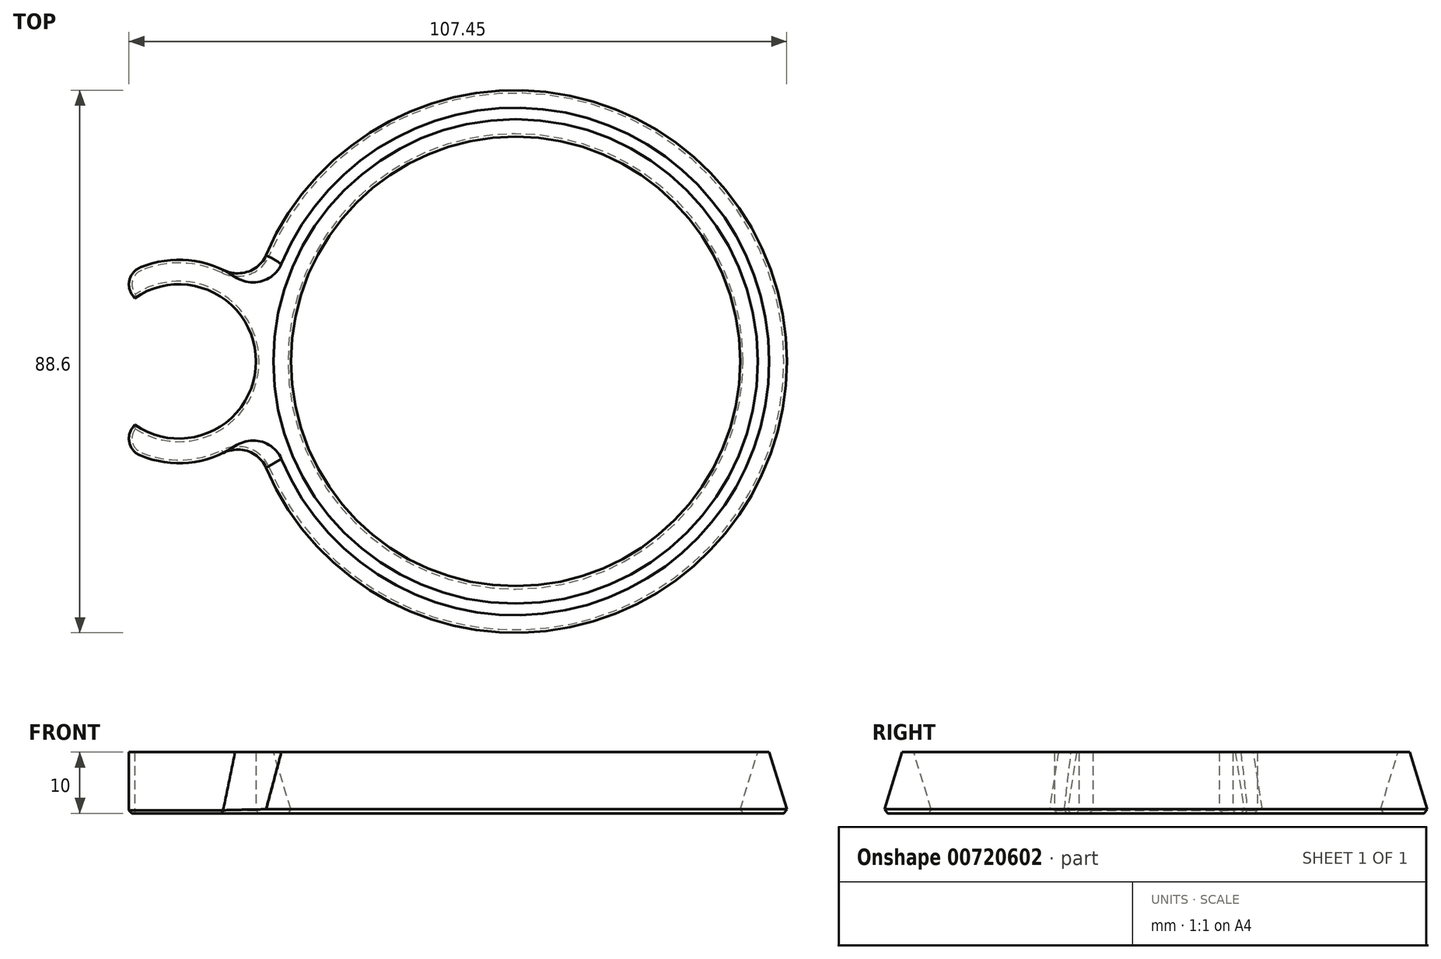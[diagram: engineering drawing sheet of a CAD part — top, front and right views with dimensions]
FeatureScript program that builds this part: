
annotation { "Feature Type Name" : "Feature", "Feature Type Description" : "" }
export const myFeature = defineFeature(function(context is Context, id is Id, definition is map)
    precondition{}
    {
        {
            var Q0;
            Q0=qCreatedBy(makeId("Top.planeOp"),FACE);
            var sketch = newSketch(context, id + "F0", { "sketchPlane" : qUnion([Q0])});
            skCircle(sketch, "E0", {"center": v(0, 0) * mm, "radius": 36.5 * mm});
            skCircle(sketch, "E1", {"center": v(0, 0) * mm, "radius": 44.5 * mm});
            skSolve(sketch);
        }
        {
            var Q0;
            Q0 = qSketchRegion(id + "F0", true);
            extrude(context, id + "F1", {"entities" : qUnion([Q0]), "depth" : 10 * mm, "offsetDistance" : 25 * mm, "hasDraft" : true, "draftAngle" : 17 * degree, "draftPullDirection" : true});
        }
        {
            var Q0;
            Q0=qCreatedBy(makeId("Top.planeOp"),FACE);
            var sketch = newSketch(context, id + "F2", { "sketchPlane" : qUnion([Q0])});
            skArc(sketch, "E2", {"start": v(-62.23, -10.32) * mm, "mid": v(-42.4, 0) * mm, "end": v(-62.23, 10.32) * mm});
            skArc(sketch, "E3", {"start": v(-39.22, 5.15) * mm, "mid": v(-49.74, 15.75) * mm, "end": v(-64.52, 13.6) * mm});
            skLineSegment(sketch, "E4", {"start": v(-62.23, 10.32) * mm, "end": v(-64.52, 13.6) * mm});
            skLineSegment(sketch, "E5", {"start": v(-64.52, 13.6) * mm, "end": v(-64.52, -13.6) * mm, "construction": true});
            skLineSegment(sketch, "E6", {"start": v(-64.52, -13.6) * mm, "end": v(-62.23, -10.32) * mm});
            skArc(sketch, "E7.0", {"start": v(-39.22, 5.15) * mm, "mid": v(-39.56, 0) * mm, "end": v(-39.22, -5.15) * mm});
            skArc(sketch, "E8.trimOffspring", {"start": v(-64.52, -13.6) * mm, "mid": v(-49.74, -15.75) * mm, "end": v(-39.22, -5.15) * mm});
            skSolve(sketch);
        }
        {
            var Q0;
            Q0=makeQuery(id+"F2.imprint","IMPRINT",FACE,{"disambiguationData":[TD([[makeQuery(id+"F2.imprint","IMPRINT",EDGE,{"derivedFrom":sQuery(id+"F2.wireOp",EDGE,"E2")}),-1.0]])]});
            var Q1;
            Q1=sQuery(id+"F2.wireOp",EDGE,"E5");
            extrude(context, id + "F3", {"entities" : qUnion([Q0]), "operationType" : NewBodyOperationType.ADD, "surfaceOperationType" : NewSurfaceOperationType.ADD, "surfaceEntities" : qUnion([Q1]), "depth" : 10 * mm, "offsetDistance" : 25 * mm});
        }
        {
            var Q0;
            Q0=qCreatedBy(makeId("Top.planeOp"),FACE);
            var sketch = newSketch(context, id + "F4", { "sketchPlane" : qUnion([Q0])});
            skArc(sketch, "E9.0", {"start": v(-62.23, -10.32) * mm, "mid": v(-42.4, 0) * mm, "end": v(-62.23, 10.32) * mm});
            skLineSegment(sketch, "E10", {"start": v(-62.23, 10.32) * mm, "end": v(-62.23, -10.32) * mm});
            skSolve(sketch);
        }
        {
            var Q0;
            Q0 = qSketchRegion(id + "F4", true);
            extrude(context, id + "F5", {"entities" : qUnion([Q0]), "operationType" : NewBodyOperationType.REMOVE, "depth" : 25 * mm, "offsetDistance" : 25 * mm});
        }
        {
            var Q0;
            Q0=makeQuery(id+"F3.boolean.opBoolean","INTERSECT",EDGE,{"derivedFrom":[makeQuery(id+"F1.opExtrude","SWEPT_FACE",FACE,{"disambiguationData":[OSD([sQuery(id+"F0.wireOp",EDGE,"E1")])]}),makeQuery(id+"F3.opExtrude","SWEPT_FACE",FACE,{"disambiguationData":[OSD([sQuery(id+"F2.wireOp",EDGE,"E8.trimOffspring")])]})]});
            var Q1;
            Q1=makeQuery(id+"F3.boolean.opBoolean","INTERSECT",EDGE,{"derivedFrom":[makeQuery(id+"F1.opExtrude","SWEPT_FACE",FACE,{"disambiguationData":[OSD([sQuery(id+"F0.wireOp",EDGE,"E1")])]}),makeQuery(id+"F3.opExtrude","SWEPT_FACE",FACE,{"disambiguationData":[OSD([sQuery(id+"F2.wireOp",EDGE,"E3")])]})]});
            fillet(context, id + "F6", {"entities" : qUnion([Q0, Q1]), "radius" : 5 * mm, "tangentPropagation" : true, "allowEdgeOverflow" : false});
        }
        {
            var Q0;
            Q0=makeQuery(id+"F3.opExtrude","SWEPT_EDGE",EDGE,{"disambiguationData":[OSD([sQuery(id+"F2.wireOp",EDGE,"E6"),sQuery(id+"F2.wireOp",EDGE,"E8.trimOffspring")])]});
            var Q1;
            Q1=makeQuery(id+"F3.opExtrude","SWEPT_EDGE",EDGE,{"disambiguationData":[OSD([sQuery(id+"F2.wireOp",EDGE,"E3"),sQuery(id+"F2.wireOp",EDGE,"E4")])]});
            fillet(context, id + "F7", {"entities" : qUnion([Q0, Q1]), "radius" : 3 * mm, "tangentPropagation" : true, "allowEdgeOverflow" : false});
        }
        {
            var Q0;
            Q0=makeQuery(id+"F3.boolean.opBoolean","MERGE",FACE,{"derivedFrom":[makeQuery(id+"F1.opExtrude","CAP_FACE",FACE,{"disambiguationData":[OSD([sQuery(id+"F0.wireOp",EDGE,"E0"),sQuery(id+"F0.wireOp",EDGE,"E1")])],"isStart":true}),makeQuery(id+"F3.opExtrude","CAP_FACE",FACE,{"disambiguationData":[OSD([sQuery(id+"F2.wireOp",EDGE,"E2"),sQuery(id+"F2.wireOp",EDGE,"E3"),sQuery(id+"F2.wireOp",EDGE,"E4"),sQuery(id+"F2.wireOp",EDGE,"E6"),sQuery(id+"F2.wireOp",EDGE,"E7.0"),sQuery(id+"F2.wireOp",EDGE,"E8.trimOffspring")])],"isStart":true})]});
            chamfer(context, id + "F8", {"entities" : qUnion([Q0]), "width" : 0.5 * mm, "tangentPropagation" : true});
        }
    });
